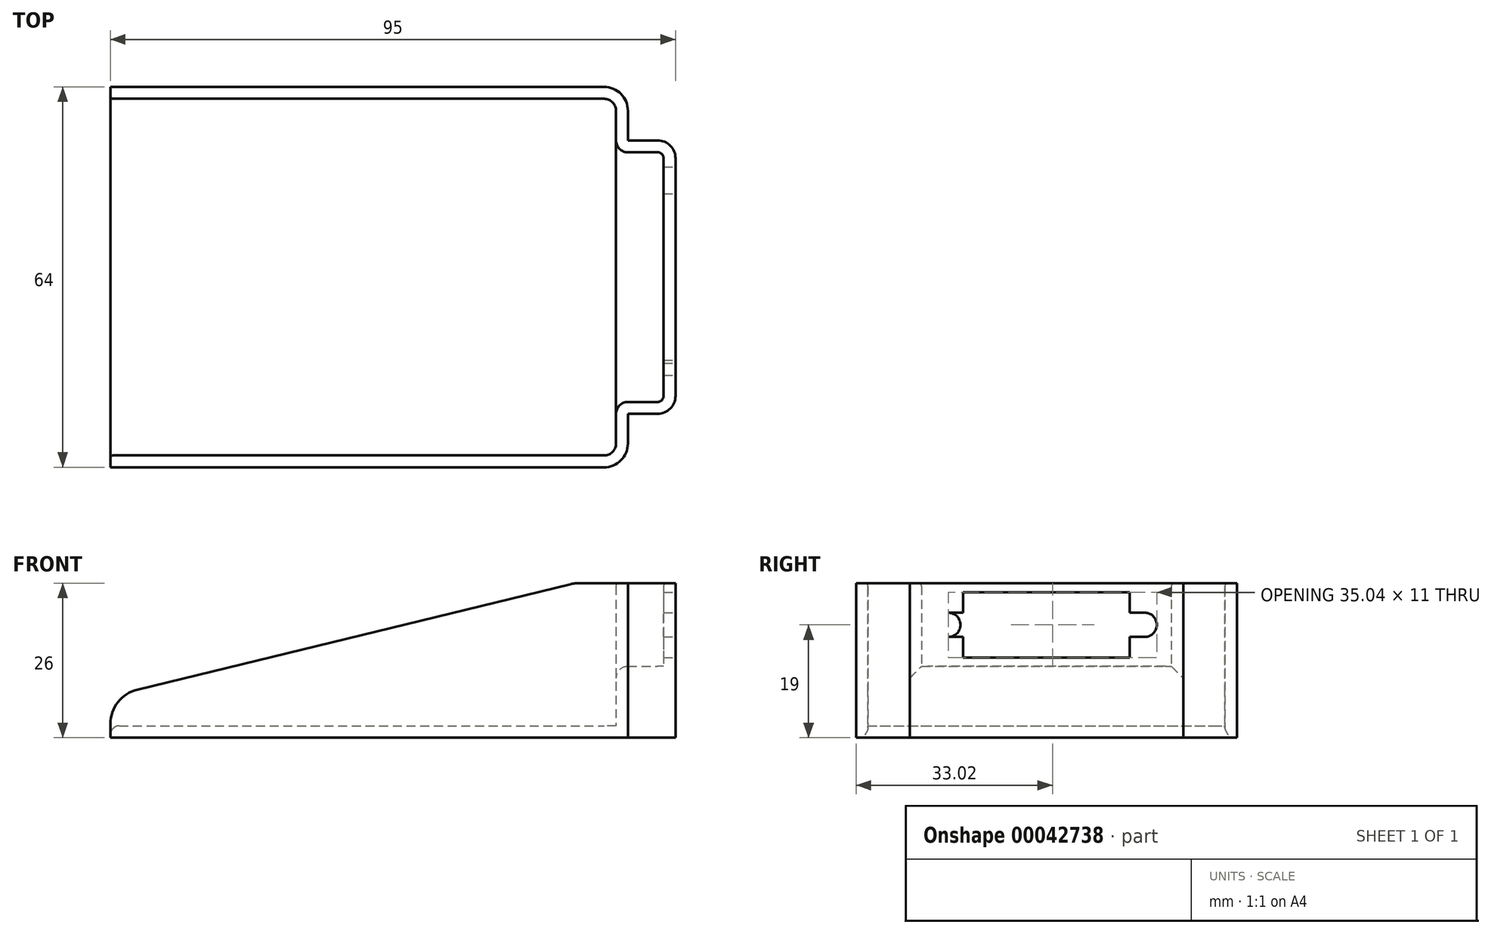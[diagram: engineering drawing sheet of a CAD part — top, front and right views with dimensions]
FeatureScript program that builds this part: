
annotation { "Feature Type Name" : "Feature", "Feature Type Description" : "" }
export const myFeature = defineFeature(function(context is Context, id is Id, definition is map)
    precondition{}
    {
        {
            var Q0;
            Q0=qCreatedBy(makeId("Top.planeOp"),FACE);
            var sketch = newSketch(context, id + "F0", { "sketchPlane" : qUnion([Q0])});
            skLineSegment(sketch, "E0.rect.bottom", {"start": v(-42.5, -30) * mm, "end": v(40.5, -30) * mm});
            skLineSegment(sketch, "E0.rect.top", {"start": v(-42.5, 30) * mm, "end": v(40.5, 30) * mm});
            skLineSegment(sketch, "E0.rect.left", {"start": v(-42.5, -30) * mm, "end": v(-42.5, 30) * mm});
            skLineSegment(sketch, "E0.rect.right", {"start": v(42.5, -28) * mm, "end": v(42.5, -23) * mm});
            skPoint(sketch, "E0.rect.middle", {"position": v(0, 0) * mm});
            skLineSegment(sketch, "E1.rect.bottom", {"start": v(44.5, 21) * mm, "end": v(49.5, 21) * mm});
            skLineSegment(sketch, "E1.rect.top", {"start": v(44.5, -21) * mm, "end": v(49.5, -21) * mm});
            skLineSegment(sketch, "E1.rect.right", {"start": v(50.5, 20) * mm, "end": v(50.5, -20) * mm});
            skPoint(sketch, "E1.rect.middle", {"position": v(46.5, 0) * mm});
            skLineSegment(sketch, "E2", {"start": v(42.5, 23) * mm, "end": v(42.5, 28) * mm});
            skPoint(sketch, "E3.visualSharp", {"position": v(42.5, 30) * mm});
            skArc(sketch, "E3.filletArc", {"start": v(42.5, 28) * mm, "mid": v(41.91, 29.41) * mm, "end": v(40.5, 30) * mm});
            skPoint(sketch, "E4.visualSharp", {"position": v(42.5, 21) * mm});
            skArc(sketch, "E4.filletArc", {"start": v(42.5, 23) * mm, "mid": v(43.09, 21.59) * mm, "end": v(44.5, 21) * mm});
            skPoint(sketch, "E5.visualSharp", {"position": v(42.5, -30) * mm});
            skArc(sketch, "E5.filletArc", {"start": v(40.5, -30) * mm, "mid": v(41.91, -29.41) * mm, "end": v(42.5, -28) * mm});
            skPoint(sketch, "E6.visualSharp", {"position": v(42.5, -21) * mm});
            skArc(sketch, "E6.filletArc", {"start": v(44.5, -21) * mm, "mid": v(43.09, -21.59) * mm, "end": v(42.5, -23) * mm});
            skPoint(sketch, "E7.visualSharp", {"position": v(50.5, -21) * mm});
            skArc(sketch, "E7.filletArc", {"start": v(49.5, -21) * mm, "mid": v(50.2, -20.7) * mm, "end": v(50.5, -20) * mm});
            skPoint(sketch, "E8.visualSharp", {"position": v(50.5, 21) * mm});
            skArc(sketch, "E8.filletArc", {"start": v(50.5, 20) * mm, "mid": v(50.2, 20.7) * mm, "end": v(49.5, 21) * mm});
            skLineSegment(sketch, "E9.0", {"start": v(-42.5, -32) * mm, "end": v(40.5, -32) * mm});
            skLineSegment(sketch, "E9.1", {"start": v(44.5, 23) * mm, "end": v(49.5, 23) * mm});
            skLineSegment(sketch, "E9.2", {"start": v(44.5, 23) * mm, "end": v(44.5, 28) * mm});
            skArc(sketch, "E9.3", {"start": v(44.5, 28) * mm, "mid": v(43.33, 30.83) * mm, "end": v(40.5, 32) * mm});
            skLineSegment(sketch, "E9.4", {"start": v(-42.5, 32) * mm, "end": v(40.5, 32) * mm});
            skArc(sketch, "E9.5", {"start": v(52.5, 20) * mm, "mid": v(51.62, 22.12) * mm, "end": v(49.5, 23) * mm});
            skLineSegment(sketch, "E9.6", {"start": v(52.5, 20) * mm, "end": v(52.5, -20) * mm});
            skArc(sketch, "E9.7", {"start": v(49.5, -23) * mm, "mid": v(51.62, -22.12) * mm, "end": v(52.5, -20) * mm});
            skLineSegment(sketch, "E9.8", {"start": v(44.5, -23) * mm, "end": v(49.5, -23) * mm});
            skLineSegment(sketch, "E9.9", {"start": v(44.5, -28) * mm, "end": v(44.5, -23) * mm});
            skArc(sketch, "E9.10", {"start": v(40.5, -32) * mm, "mid": v(43.33, -30.83) * mm, "end": v(44.5, -28) * mm});
            skLineSegment(sketch, "E10", {"start": v(-42.5, 32) * mm, "end": v(-42.5, 30) * mm});
            skLineSegment(sketch, "E11", {"start": v(-42.5, -32) * mm, "end": v(-42.5, -30) * mm});
            skSolve(sketch);
        }
        {
            var Q0;
            Q0=makeQuery(id+"F0.imprint","IMPRINT",FACE,{"disambiguationData":[TD([[makeQuery(id+"F0.imprint","IMPRINT",EDGE,{"derivedFrom":sQuery(id+"F0.wireOp",EDGE,"E0.rect.bottom")}),-1.0]])]});
            extrude(context, id + "F1", {"entities" : qUnion([Q0]), "depth" : 26 * mm});
        }
        {
            var Q0;
            Q0 = qSketchRegion(id + "F0", true);
            extrude(context, id + "F2", {"entities" : qUnion([Q0]), "operationType" : NewBodyOperationType.ADD, "depth" : 2 * mm});
        }
        {
            var Q0;
            Q0=makeQuery(id+"F1.opExtrude","SWEPT_FACE",FACE,{"disambiguationData":[OSD([sQuery(id+"F0.wireOp",EDGE,"E9.0")])]});
            var sketch = newSketch(context, id + "F3", { "sketchPlane" : qUnion([Q0])});
            skLineSegment(sketch, "E12.bottom", {"start": v(40.5, 0) * mm, "end": v(-42.5, 0) * mm});
            skLineSegment(sketch, "E12.top", {"start": v(40.5, 26) * mm, "end": v(-42.5, 26) * mm});
            skLineSegment(sketch, "E12.left", {"start": v(40.5, 0) * mm, "end": v(40.5, 26) * mm});
            skLineSegment(sketch, "E12.right", {"start": v(-42.5, 0) * mm, "end": v(-42.5, 2.29) * mm});
            skLineSegment(sketch, "E13", {"start": v(34.8, 25.83) * mm, "end": v(-37.92, 8.12) * mm});
            skLineSegment(sketch, "E14", {"start": v(-42.5, 7) * mm, "end": v(-42.5, 26) * mm});
            skLineSegment(sketch, "E15", {"start": v(36.22, 26) * mm, "end": v(40.5, 26) * mm});
            skPoint(sketch, "E16.visualSharp", {"position": v(-42.5, 7) * mm});
            skArc(sketch, "E16.filletArc", {"start": v(-37.92, 8.12) * mm, "mid": v(-41.22, 6) * mm, "end": v(-42.5, 2.29) * mm});
            skPoint(sketch, "E17.visualSharp", {"position": v(35.5, 26) * mm});
            skArc(sketch, "E17.filletArc", {"start": v(36.22, 26) * mm, "mid": v(35.5, 25.96) * mm, "end": v(34.8, 25.83) * mm});
            skSolve(sketch);
        }
        {
            var Q0;
            Q0=makeQuery(id+"F3.imprint","IMPRINT",FACE,{"disambiguationData":[TD([[makeQuery(id+"F3.imprint","IMPRINT",EDGE,{"derivedFrom":sQuery(id+"F3.wireOp",EDGE,"E12.top")}),-1.0]])]});
            extrude(context, id + "F4", {"entities" : qUnion([Q0]), "operationType" : NewBodyOperationType.REMOVE, "oppositeDirection" : true, "depth" : 64 * mm});
        }
        {
            var Q0;
            Q0=makeQuery(id+"F1.opExtrude","SWEPT_FACE",FACE,{"disambiguationData":[OSD([sQuery(id+"F0.wireOp",EDGE,"E9.6")])]});
            var sketch = newSketch(context, id + "F5", { "sketchPlane" : qUnion([Q0])});
            skLineSegment(sketch, "E18", {"start": v(-20, 19) * mm, "end": v(20, 19) * mm, "construction": true});
            skLineSegment(sketch, "E19", {"start": v(-20, 19) * mm, "end": v(-20, 0) * mm, "construction": true});
            skLineSegment(sketch, "E20.rect.bottom", {"start": v(14, 24.5) * mm, "end": v(-14, 24.5) * mm});
            skLineSegment(sketch, "E20.rect.top", {"start": v(14, 13.5) * mm, "end": v(-14, 13.5) * mm});
            skLineSegment(sketch, "E20.rect.left", {"start": v(14, 24.5) * mm, "end": v(14, 13.5) * mm});
            skLineSegment(sketch, "E20.rect.right", {"start": v(-14, 24.5) * mm, "end": v(-14, 21.04) * mm});
            skPoint(sketch, "E20.rect.middle", {"position": v(0, 19) * mm});
            skLineSegment(sketch, "E21", {"start": v(-20, 19) * mm, "end": v(0, 19) * mm, "construction": true});
            skLineSegment(sketch, "E22", {"start": v(0, 19) * mm, "end": v(16.5, 19) * mm, "construction": true});
            skLineSegment(sketch, "E23", {"start": v(-16.5, 21.04) * mm, "end": v(-14, 21.04) * mm});
            skLineSegment(sketch, "E24", {"start": v(-16.5, 16.96) * mm, "end": v(-14, 16.96) * mm});
            skLineSegment(sketch, "E25.MirrorCS", {"start": v(16.5, 21.04) * mm, "end": v(14, 21.04) * mm});
            skLineSegment(sketch, "E26.MirrorCS", {"start": v(14, 24.5) * mm, "end": v(14, 21.04) * mm});
            skLineSegment(sketch, "E27.MirrorCS", {"start": v(16.5, 16.96) * mm, "end": v(14, 16.96) * mm});
            skArc(sketch, "E28", {"start": v(-16.5, 21.04) * mm, "mid": v(-14.46, 19) * mm, "end": v(-16.5, 16.96) * mm});
            skArc(sketch, "E29", {"start": v(-16.5, 16.96) * mm, "mid": v(-18.54, 19) * mm, "end": v(-16.5, 21.04) * mm});
            skArc(sketch, "E30", {"start": v(16.5, 21.04) * mm, "mid": v(14.46, 19) * mm, "end": v(16.5, 16.96) * mm});
            skArc(sketch, "E31", {"start": v(16.5, 16.96) * mm, "mid": v(18.54, 19) * mm, "end": v(16.5, 21.04) * mm});
            skLineSegment(sketch, "E32", {"start": v(14, 16.96) * mm, "end": v(14, 13.5) * mm});
            skLineSegment(sketch, "E33", {"start": v(14, 21.04) * mm, "end": v(14, 16.96) * mm});
            skLineSegment(sketch, "E34", {"start": v(-14, 21.04) * mm, "end": v(-14, 16.96) * mm});
            skLineSegment(sketch, "E35", {"start": v(-14, 16.96) * mm, "end": v(-14, 13.5) * mm});
            skSolve(sketch);
        }
        {
            var Q0;
            Q0=makeQuery(id+"F5.imprint","IMPRINT",FACE,{"disambiguationData":[TD([[makeQuery(id+"F5.imprint","IMPRINT",EDGE,{"derivedFrom":sQuery(id+"F5.wireOp",EDGE,"E25.MirrorCS")}),1.0]])]});
            var Q1;
            Q1=makeQuery(id+"F5.imprint","IMPRINT",FACE,{"disambiguationData":[TD([[makeQuery(id+"F5.imprint","IMPRINT",EDGE,{"derivedFrom":sQuery(id+"F5.wireOp",EDGE,"E20.rect.bottom")}),1.0]])]});
            var Q2;
            Q2=makeQuery(id+"F5.imprint","IMPRINT",FACE,{"disambiguationData":[TD([[makeQuery(id+"F5.imprint","IMPRINT",EDGE,{"derivedFrom":sQuery(id+"F5.wireOp",EDGE,"E23")}),-1.0]])]});
            var Q3;
            Q3=makeQuery(id+"F5.imprint","IMPRINT",FACE,{"disambiguationData":[TD([[makeQuery(id+"F5.imprint","IMPRINT",EDGE,{"derivedFrom":sQuery(id+"F5.wireOp",EDGE,"E28")}),-1.0]])]});
            var Q4;
            Q4=makeQuery(id+"F5.imprint","IMPRINT",FACE,{"disambiguationData":[TD([[makeQuery(id+"F5.imprint","IMPRINT",EDGE,{"derivedFrom":sQuery(id+"F5.wireOp",EDGE,"E30")}),1.0]])]});
            extrude(context, id + "F6", {"entities" : qUnion([Q0, Q1, Q2, Q3, Q4]), "operationType" : NewBodyOperationType.REMOVE, "endBound" : BoundingType.THROUGH_ALL, "oppositeDirection" : true, "depth" : 2 * mm});
        }
        {
            var Q0;
            Q0=makeQuery(id+"F4.boolean.opBoolean","COPY",EDGE,{"derivedFrom":makeQuery(id+"F4.opExtrude","CAP_EDGE",EDGE,{"disambiguationData":[OSD([sQuery(id+"F3.wireOp",EDGE,"E13")])],"isStart":true})});
            var Q1;
            Q1=makeQuery(id+"F4.boolean.opBoolean","COPY",EDGE,{"derivedFrom":makeQuery(id+"F4.opExtrude","CAP_EDGE",EDGE,{"disambiguationData":[OSD([sQuery(id+"F3.wireOp",EDGE,"E13")])],"isStart":false})});
            var Q2;
            Q2=makeQuery(id+"F4.boolean.opBoolean","INTERSECT",EDGE,{"derivedFrom":[makeQuery(id+"F1.opExtrude","SWEPT_FACE",FACE,{"disambiguationData":[OSD([sQuery(id+"F0.wireOp",EDGE,"E0.rect.top")])]}),makeQuery(id+"F4.opExtrude","SWEPT_FACE",FACE,{"disambiguationData":[OSD([sQuery(id+"F3.wireOp",EDGE,"E13")])]})]});
            fillet(context, id + "F7", {"entities" : qUnion([Q0, Q1, Q2]), "radius" : 0.5 * mm, "tangentPropagation" : true, "allowEdgeOverflow" : false});
        }
        {
            var Q0;
            Q0=makeQuery(id+"F2.opExtrude","CAP_EDGE",EDGE,{"disambiguationData":[OSD([sQuery(id+"F0.wireOp",EDGE,"E0.rect.left"),sQuery(id+"F0.wireOp",EDGE,"E10"),sQuery(id+"F0.wireOp",EDGE,"E11")])],"isStart":false});
            fillet(context, id + "F8", {"entities" : qUnion([Q0]), "radius" : 1.5 * mm, "tangentPropagation" : true, "allowEdgeOverflow" : false});
        }
        {
            var Q0;
            Q0=makeQuery(id+"F2.opExtrude","CAP_FACE",FACE,{"disambiguationData":[OSD([sQuery(id+"F0.wireOp",EDGE,"E0.rect.left"),sQuery(id+"F0.wireOp",EDGE,"E9.0"),sQuery(id+"F0.wireOp",EDGE,"E9.1"),sQuery(id+"F0.wireOp",EDGE,"E9.2"),sQuery(id+"F0.wireOp",EDGE,"E9.3"),sQuery(id+"F0.wireOp",EDGE,"E9.4"),sQuery(id+"F0.wireOp",EDGE,"E9.5"),sQuery(id+"F0.wireOp",EDGE,"E9.6"),sQuery(id+"F0.wireOp",EDGE,"E9.7"),sQuery(id+"F0.wireOp",EDGE,"E9.8"),sQuery(id+"F0.wireOp",EDGE,"E9.9"),sQuery(id+"F0.wireOp",EDGE,"E9.10"),sQuery(id+"F0.wireOp",EDGE,"E10"),sQuery(id+"F0.wireOp",EDGE,"E11")])],"isStart":false});
            var sketch = newSketch(context, id + "F9", { "sketchPlane" : qUnion([Q0])});
            skLineSegment(sketch, "E36", {"start": v(42.5, -23) * mm, "end": v(42.5, 23) * mm});
            skSolve(sketch);
        }
        {
            var Q0;
            Q0=makeQuery(id+"F9.imprint","IMPRINT",FACE,{"disambiguationData":[TD([[makeQuery(id+"F9.imprint","IMPRINT",EDGE,{"derivedFrom":sQuery(id+"F9.wireOp",EDGE,"E36")}),-1.0]])]});
            extrude(context, id + "F10", {"entities" : qUnion([Q0]), "operationType" : NewBodyOperationType.ADD, "depth" : 10 * mm});
        }
        {
            var Q0;
            Q0=makeQuery(id+"F10.opExtrude","CAP_EDGE",EDGE,{"disambiguationData":[OSD([sQuery(id+"F9.wireOp",EDGE,"E36")])],"isStart":false});
            fillet(context, id + "F11", {"entities" : qUnion([Q0]), "radius" : 2 * mm, "tangentPropagation" : true, "allowEdgeOverflow" : false});
        }
    });
